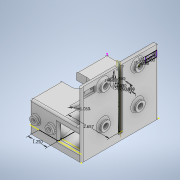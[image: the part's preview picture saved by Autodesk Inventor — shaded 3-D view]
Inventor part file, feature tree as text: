
AUTODESK INVENTOR PART (.ipt)
format: ipt  version: 2020 (Build 240168000, 168)  size: 635,904 bytes
history: native  units: in
note: dims shown in document units (in); Inventor stores cm internally (conversion verified against a paired STEP export)
features: sketch x19, extrude x15, hole x6, fillet x3, mirror x2, plane x1
ambient origin geometry x8: Origin, YZ Plane, XZ Plane, XY Plane, X Axis, Y Axis, Z Axis, Center Point
bodies: Solid1 (feature_tree)
feature tree (46):
  extrude  "Extrusion1"  Depth=5.0299in
  extrude  "Extrusion2"  Depth=0.375in
  extrude  "Extrusion3"  Depth=2.8543in
  sketch  "Sketch5"  dims[d24=5.315in d25=4.5472in]
  extrude  "Extrusion4"  Depth=4.5472in
  extrude  "Extrusion5"  Depth=0.25in
  extrude  "Extrusion6"  Depth=2.6575in
  hole  "Hole2"  [1 undecoded]
  extrude  "Extrusion7"  Depth=0.5in
  extrude  "Extrusion8"  Depth=1.5in
  extrude  "Extrusion9"  Depth=0.312in
  extrude  "Extrusion10"  Depth=0.312in
  hole  "Hole3"  [1 undecoded]
  extrude  "Extrusion11"  Depth=1.5in TaperAngle=0.0deg
  extrude  "Extrusion12"  Depth=1.125in
  hole  "Hole4"  [1 undecoded]
  sketch  "Sketch17"  dims[d61=1.49in d62=2.25in]
  extrude  "Extrusion13"  TaperAngle=90.0deg  [1 undecoded]
  hole  "Hole5"  [1 undecoded]
  plane  "Work Plane1"
  mirror  "Mirror1"
  extrude  "Extrusion14"  TaperAngle=0.0deg  [1 undecoded]
  fillet  "Fillet1"  Radius=0.625in
  sketch  "Sketch20"  dims[d67=0.332in d68=0.375in d69=0.119in d70=0.25in d71=0.5635in d72=0.375in d73=0.0in d74=0.0in d75=0.0in d76=0.625in]
  extrude  "Extrusion15"  Depth=0.25in
  fillet  "Fillet2"  Radius=0.625in
  hole  "Hole6"  [1 undecoded]
  mirror  "Mirror2"
  fillet  "Fillet3"  Radius=0.36in
  hole  "Hole7"  [1 undecoded]
  sketch  "Sketch18"  dims[d63=2.25in d64=90.0deg]
  sketch  "Sketch1"  dims[d0=3.3654in d1=5.0299in]
  sketch  "Sketch3"  dims[d3=45.0deg d4=0.375in]
  sketch  "Sketch4"  dims[d5=0.5in d6=0.0in d23=2.8543in]
  sketch  "Sketch6"  dims[d26=0.1in d27=0.0in d28=0.25in]
  sketch  "Sketch7"  dims[d29=0.1in d30=0.0in d31=2.6575in]
  sketch  "Sketch9"  dims[d32=1.05in d33=1.25in]
  sketch  "Sketch10"  dims[d34=1.4685in d35=0.0in d36=0.5in]
  sketch  "Sketch11"  dims[d37=5.03in d38=0.0in d39=1.5in]
  sketch  "Sketch12"  dims[d40=1.0in d41=0.0in d42=0.312in]
  sketch  "Sketch13"  dims[d43=0.0in d44=0.312in]
  sketch  "Sketch14"  dims[d45=0.177in d46=0.75in d47=0.385in d48=0.25in d49=0.5635in d50=1.378in d51=0.0in d52=1.4685in d53=0.0in]
  sketch  "Sketch15"  dims[d54=1.9685in d55=0.0in d56=1.5in d57=0.0in]
  sketch  "Sketch16"  dims[d58=3.75in d59=0.0in d60=1.125in]
  sketch  "Sketch19"  dims[d65=2.25in d66=90.0deg]
  sketch  "Sketch21"  dims[d77=0.625in d78=0.625in d79=0.625in d80=0.2in d81=0.0in d82=0.36in d83=1.125in d84=0.185in d85=0.37in d86=0.09in d87=0.375in d88=0.119in d89=0.25in d90=0.5635in d91=0.375in d92=0.0in d93=0.375in d94=0.0in d95=0.25in d96=0.5in d97=0.375in d98=0.125in d99=0.0in d100=0.129in d101=0.198in d102=0.225in d103=0.188in d104=0.5635in d105=0.375in d106=0.0in d107=0.125in d108=0.125in d109=1.0in d110=1.0in d111=0.5in d112=1.5in d113=0.0in d114=0.931in d115=0.5in d116=1.0in d117=0.0in d120=0.1875in d121=0.0in d122=0.0625in d123=0.266in d124=0.75in d125=0.438in d126=0.25in d127=0.5635in d128=0.25in d129=0.0in d130=0.5in d131=90.0deg d132=0.5in d133=90.0deg d134=0.5in d135=0.5in d136=0.0625in d137=1.0in d138=0.5in d139=0.5in d140=90.0deg d141=0.5in d142=1.0in d143=180.0deg d144=1.0in d145=90.0deg d146=1.0in d147=0.266in d148=0.75in d149=0.438in d150=0.25in d151=0.5635in d152=1.0in d153=0.8108in]
note: 8 required parameter values undecoded (feature->parameter linkage not recoverable at this tier; creation-order binding heuristic only, values carry confidence <= 0.55)
